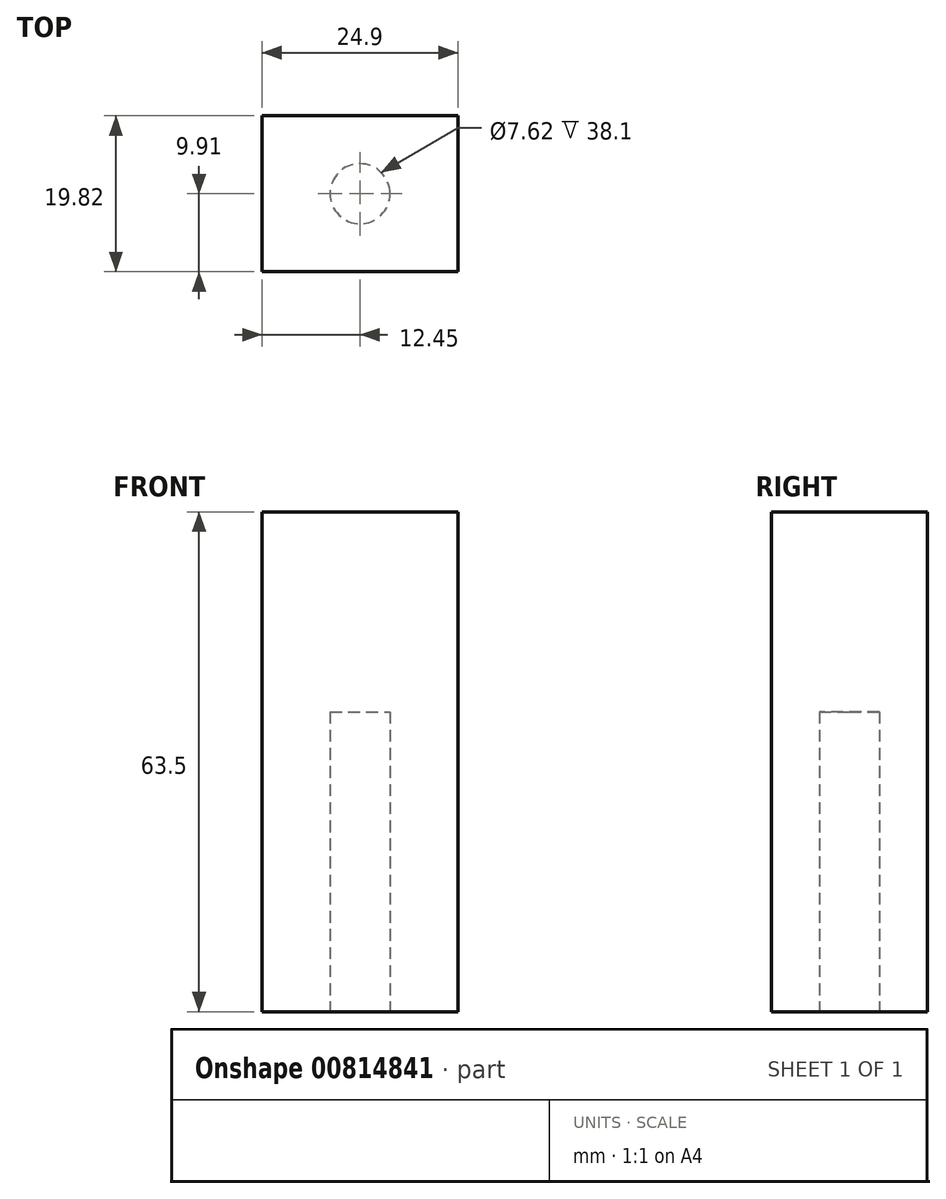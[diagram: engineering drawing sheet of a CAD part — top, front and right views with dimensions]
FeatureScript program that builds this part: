
annotation { "Feature Type Name" : "Feature", "Feature Type Description" : "" }
export const myFeature = defineFeature(function(context is Context, id is Id, definition is map)
    precondition{}
    {
        {
            var Q0;
            Q0=qCreatedBy(makeId("Top.planeOp"),FACE);
            var sketch = newSketch(context, id + "F0", { "sketchPlane" : qUnion([Q0])});
            skPoint(sketch, "E0.middle", {"position": v(0, 0) * mm});
            skCircle(sketch, "E1", {"center": v(-6.35, 0) * mm, "radius": 2.16 * mm, "construction": true});
            skCircle(sketch, "E2", {"center": v(6.35, 0) * mm, "radius": 2.16 * mm, "construction": true});
            skLineSegment(sketch, "E3.bottom", {"start": v(-12.45, 9.9) * mm, "end": v(12.45, 9.9) * mm});
            skLineSegment(sketch, "E3.top", {"start": v(-12.45, -9.9) * mm, "end": v(12.45, -9.9) * mm});
            skLineSegment(sketch, "E3.left", {"start": v(-12.45, 9.9) * mm, "end": v(-12.45, -9.9) * mm});
            skLineSegment(sketch, "E3.right", {"start": v(12.45, 9.9) * mm, "end": v(12.45, -9.9) * mm});
            skSolve(sketch);
        }
        {
            var Q0;
            Q0=makeQuery(id+"F0.imprint","IMPRINT",FACE,{"disambiguationData":[TD([[makeQuery(id+"F0.imprint","IMPRINT",EDGE,{"derivedFrom":sQuery(id+"F0.wireOp",EDGE,"E3.bottom")}),-1.0]])]});
            extrude(context, id + "F1", {"entities" : qUnion([Q0]), "endBound" : BoundingType.SYMMETRIC, "depth" : 63.5 * mm, "offsetDistance" : 25.4 * mm});
        }
        {
            var Q0;
            Q0=makeQuery(id+"F1.opExtrude","CAP_FACE",FACE,{"disambiguationData":[OSD([sQuery(id+"F0.wireOp",EDGE,"E3.bottom"),sQuery(id+"F0.wireOp",EDGE,"E3.top"),sQuery(id+"F0.wireOp",EDGE,"E3.left"),sQuery(id+"F0.wireOp",EDGE,"E3.right")])],"isStart":true});
            var sketch = newSketch(context, id + "F2", { "sketchPlane" : qUnion([Q0])});
            skCircle(sketch, "E4", {"center": v(0, 0) * mm, "radius": 3.81 * mm});
            skSolve(sketch);
        }
        {
            var Q0;
            Q0 = qSketchRegion(id + "F2", true);
            extrude(context, id + "F3", {"entities" : qUnion([Q0]), "operationType" : NewBodyOperationType.REMOVE, "oppositeDirection" : true, "depth" : 38.1 * mm, "offsetDistance" : 25.4 * mm});
        }
    });
